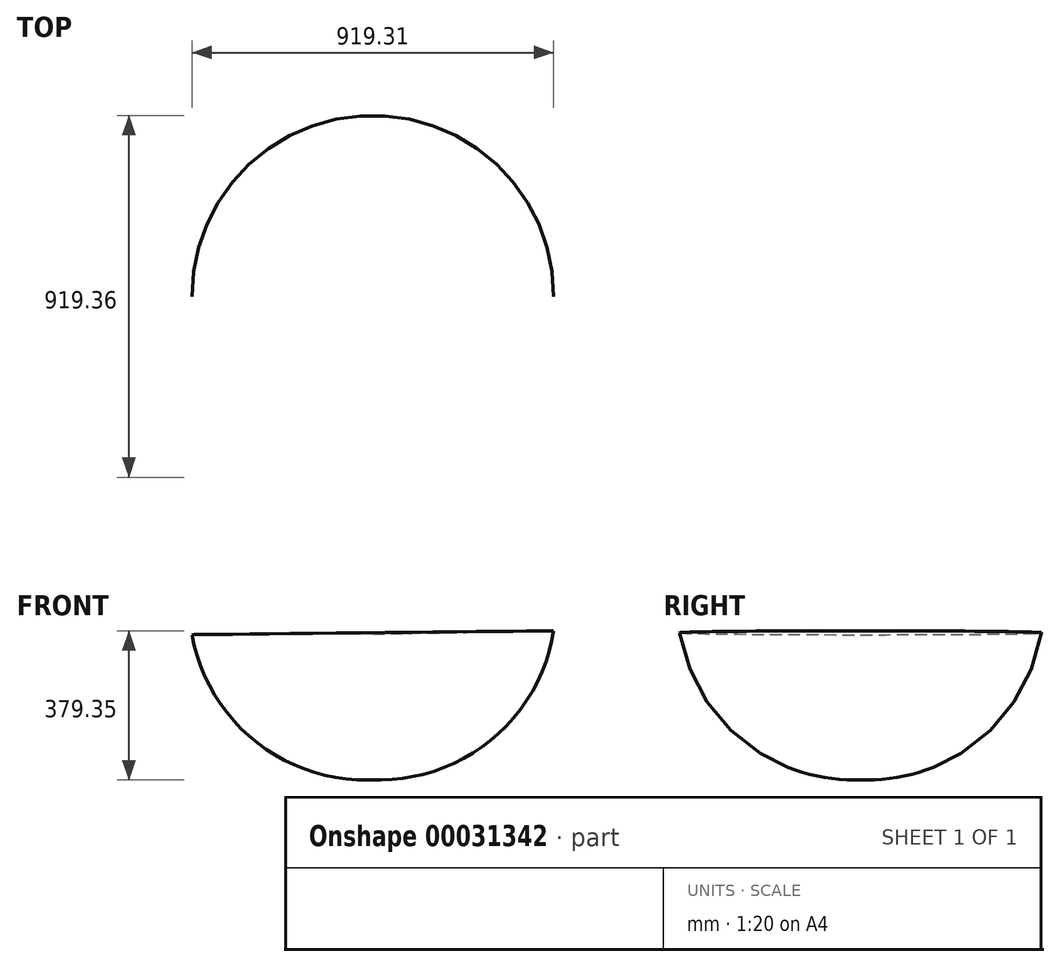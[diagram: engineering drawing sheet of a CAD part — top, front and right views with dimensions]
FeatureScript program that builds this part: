
annotation { "Feature Type Name" : "Feature", "Feature Type Description" : "" }
export const myFeature = defineFeature(function(context is Context, id is Id, definition is map)
    precondition{}
    {
        {
            var Q0;
            Q0=qCreatedBy(makeId("Front.planeOp"),FACE);
            var sketch = newSketch(context, id + "F0", { "sketchPlane" : qUnion([Q0])});
            skLineSegment(sketch, "E0", {"start": v(-45.96, 36.29) * mm, "end": v(45.96, 37.9) * mm});
            skLineSegment(sketch, "E1", {"start": v(45.96, 37.9) * mm, "end": v(45.96, -37.9) * mm});
            skLineSegment(sketch, "E2", {"start": v(45.96, -37.9) * mm, "end": v(-45.16, -37.9) * mm});
            skLineSegment(sketch, "E3", {"start": v(-45.16, -37.9) * mm, "end": v(-45.96, 36.29) * mm});
            skSolve(sketch);
        }
        {
            var Q0;
            Q0 = qSketchRegion(id + "F0", true);
            var Q1;
            Q1=sQuery(id+"F0.wireOp",EDGE,"E3");
            revolve(context, id + "F1", {"entities" : qUnion([Q0]), "axis" : qUnion([Q1]), "revolveType" : RevolveType.FULL});
        }
        {
            var Q0;
            Q0=makeQuery(id+"F1.opRevolve","SWEPT_BODY",BODY,{"disambiguationData":[OSD([sQuery(id+"F0.wireOp",EDGE,"E0"),sQuery(id+"F0.wireOp",EDGE,"E1"),sQuery(id+"F0.wireOp",EDGE,"E2"),sQuery(id+"F0.wireOp",EDGE,"E3")])]});
            var Q1;
            Q1=qCreatedBy(makeId("Origin.pointOp"),VERTEX);
            transform(context, id + "F2", {"entities" : qUnion([Q0]), "transformType" : TransformType.SCALE_UNIFORMLY, "scale" : 5, "makeCopy" : false, "scalePoint" : qUnion([Q1])});
        }
        {
            var Q0;
            Q0=makeQuery(id+"F1.opRevolve","SWEPT_FACE",FACE,{"disambiguationData":[OSD([sQuery(id+"F0.wireOp",EDGE,"E2")])]});
            fillet(context, id + "F3", {"entities" : qUnion([Q0]), "radius" : 449.02 * mm, "tangentPropagation" : true, "allowEdgeOverflow" : false});
        }
    });
